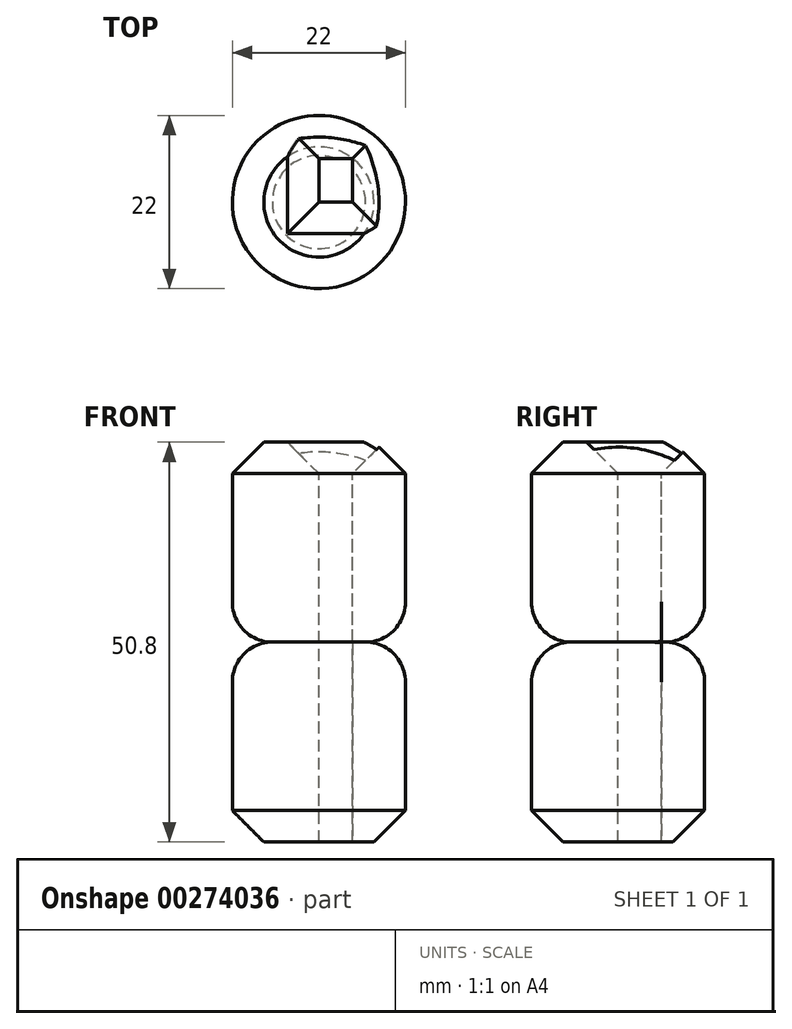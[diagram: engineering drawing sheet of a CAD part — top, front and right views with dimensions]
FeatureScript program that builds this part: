
annotation { "Feature Type Name" : "Feature", "Feature Type Description" : "" }
export const myFeature = defineFeature(function(context is Context, id is Id, definition is map)
    precondition{}
    {
        {
            var Q0;
            Q0=qCreatedBy(makeId("Top.planeOp"),FACE);
            var sketch = newSketch(context, id + "F0", { "sketchPlane" : qUnion([Q0])});
            skCircle(sketch, "E0", {"center": v(0, 0) * mm, "radius": 11 * mm});
            skSolve(sketch);
        }
        {
            var Q0;
            Q0 = qSketchRegion(id + "F0", true);
            extrude(context, id + "F1", {"entities" : qUnion([Q0]), "depth" : 25.4 * mm});
        }
        {
            var Q0;
            Q0=makeQuery(id+"F1.opExtrude","CAP_FACE",FACE,{"disambiguationData":[OSD([sQuery(id+"F0.wireOp",EDGE,"E0")])],"isStart":false});
            var sketch = newSketch(context, id + "F2", { "sketchPlane" : qUnion([Q0])});
            skLineSegment(sketch, "E1.bottom", {"start": v(0, 0) * mm, "end": v(4.26, 0) * mm});
            skLineSegment(sketch, "E1.top", {"start": v(0, 5.5) * mm, "end": v(4.26, 5.5) * mm});
            skLineSegment(sketch, "E1.left", {"start": v(0, 0) * mm, "end": v(0, 5.5) * mm});
            skLineSegment(sketch, "E1.right", {"start": v(4.26, 0) * mm, "end": v(4.26, 5.5) * mm});
            skSolve(sketch);
        }
        {
            var Q0;
            Q0=makeQuery(id+"F2.imprint","IMPRINT",FACE,{"disambiguationData":[TD([[makeQuery(id+"F2.imprint","IMPRINT",EDGE,{"derivedFrom":sQuery(id+"F2.wireOp",EDGE,"E1.bottom")}),1.0]])]});
            var Q1;
            Q1=makeQuery(id+"F1.opExtrude","CAP_FACE",FACE,{"disambiguationData":[OSD([sQuery(id+"F0.wireOp",EDGE,"E0")])],"isStart":true});
            extrude(context, id + "F3", {"entities" : qUnion([Q0, Q1]), "operationType" : NewBodyOperationType.REMOVE, "endBound" : BoundingType.THROUGH_ALL, "oppositeDirection" : true, "depth" : 16.76 * mm});
        }
        {
            var Q0;
            Q0=makeQuery(id+"F1.opExtrude","CAP_EDGE",EDGE,{"disambiguationData":[OSD([sQuery(id+"F0.wireOp",EDGE,"E0")])],"isStart":true});
            fillet(context, id + "F4", {"entities" : qUnion([Q0]), "radius" : 5.08 * mm, "tangentPropagation" : true, "allowEdgeOverflow" : false});
        }
        {
            var Q0;
            Q0=makeQuery(id+"F1.opExtrude","SWEPT_BODY",BODY,{"disambiguationData":[OSD([sQuery(id+"F0.wireOp",EDGE,"E0")])]});
            var Q1;
            Q1=makeQuery(id+"F1.opExtrude","CAP_FACE",FACE,{"disambiguationData":[OSD([sQuery(id+"F0.wireOp",EDGE,"E0")])],"isStart":true});
            mirror(context, id + "F5", {"operationType" : NewBodyOperationType.ADD, "entities" : qUnion([Q0]), "mirrorPlane" : qUnion([Q1])});
        }
        {
            var Q0;
            Q0=makeQuery(id+"F5.opPattern","COPY",EDGE,{"derivedFrom":makeQuery(id+"F1.opExtrude","CAP_EDGE",EDGE,{"disambiguationData":[OSD([sQuery(id+"F0.wireOp",EDGE,"E0")])],"isStart":false}),"instanceName":"1"});
            chamfer(context, id + "F6", {"entities" : qUnion([Q0]), "width" : 4 * mm, "tangentPropagation" : true});
        }
        {
            var Q0;
            Q0=makeQuery(id+"F1.opExtrude","CAP_FACE",FACE,{"disambiguationData":[OSD([sQuery(id+"F0.wireOp",EDGE,"E0")])],"isStart":false});
            chamfer(context, id + "F7", {"entities" : qUnion([Q0]), "width" : 4 * mm, "tangentPropagation" : true});
        }
    });
